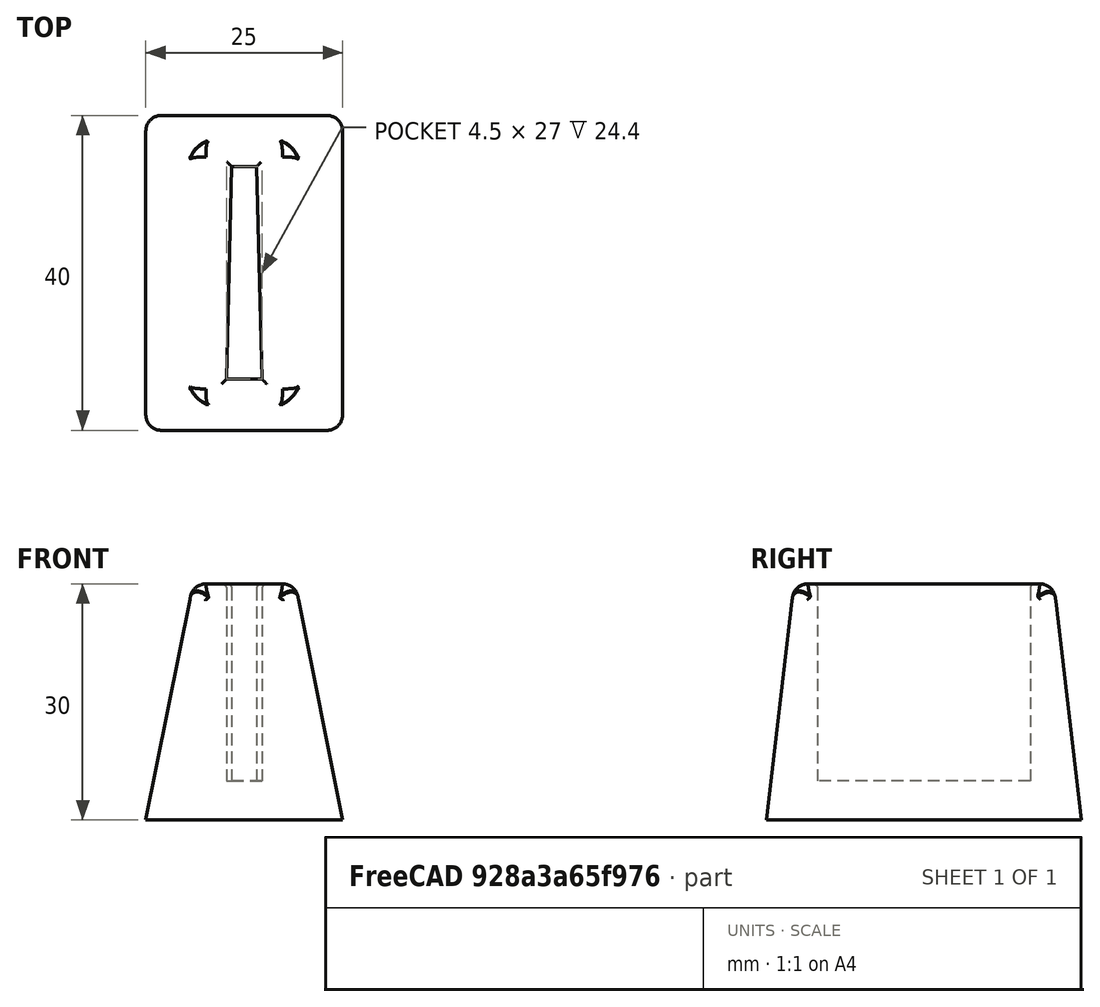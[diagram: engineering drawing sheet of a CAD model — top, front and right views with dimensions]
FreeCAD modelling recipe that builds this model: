
FCSTD DOCUMENT  (FreeCAD 0.18R16117 (Git))
Label: Porte peigne
License: All rights reserved
LicenseURL: http://en.wikipedia.org/wiki/All_rights_reserved
objects: Sketcher::SketchObject×3, PartDesign::Fillet×3, PartDesign::Pocket×2, PartDesign::Pad×1, PartDesign::Body×1
note: 13 computed .brp shape members not serialized (recipe doc carries the construction recipe); baked Part::Feature solids carry a one-line shape summary decoded from their .brp

FEATURE [Sketcher::SketchObject] Sketch
  MapMode = 5
  Placement = pos=(0,0,0) rot=(1,0,0;1.5708rad)
  Support = -> [XZ_Plane]
  sketch-geometry (6):
    g0: LineSegment StartX=-12.5 StartY=0 StartZ=0 EndX=12.5 EndY=0 EndZ=0
    g1: LineSegment StartX=12.5 StartY=0 StartZ=0 EndX=6.5 EndY=30 EndZ=0
    g2: LineSegment StartX=6.5 StartY=30 StartZ=0 EndX=-6.5 EndY=30 EndZ=0
    g3: LineSegment StartX=-6.5 StartY=30 StartZ=0 EndX=-12.5 EndY=0 EndZ=0
    g4: LineSegment [constr] StartX=-6.5 StartY=30 StartZ=0 EndX=0 EndY=30 EndZ=0
    g5: LineSegment [constr] StartX=-12.5 StartY=0 StartZ=0 EndX=0 EndY=0 EndZ=0
  constraints (17):
    c: Coincident(g0,g1)
    c: Coincident(g1,g2)
    c: Coincident(g2,g3)
    c: Coincident(g3,g0)
    c: Parallel(g2,g0)
    c: Horizontal(g0)
    c: DistanceX(g0,g0) = 25
    c: DistanceX(g2,g2) = 13
    c: DistanceY(g0,g1) = 30
    c: Coincident(g5,g0)
    c: Coincident(g4,g2)
    c: Distance(g4) = 6.5
    c: Horizontal(g4)
    c: Distance(g5) = 12.5
    c: Horizontal(g5)
    c: Vertical(g5,g4)
    c: Coincident(g5,g-1)
FEATURE [PartDesign::Pad] Pad
  Length = 40
  Length2 = 100
  Placement = pos=(0,0,0) rot=(1,0,0;1.5708rad)
  Profile = -> Sketch
  Type = 0
FEATURE [Sketcher::SketchObject] Sketch001
  ExternalGeometry = -> [Pad]
  MapMode = 5
  Placement = pos=(0,2e-14,30) rot=(0,0,1;3.14159rad)
  Support = -> [Pad]
  sketch-geometry (6):
    g0: LineSegment StartX=-2.25 StartY=33.5 StartZ=0 EndX=2.25 EndY=33.5 EndZ=0
    g1: LineSegment StartX=2.25 StartY=33.5 StartZ=0 EndX=1.575 EndY=6.5 EndZ=0
    g2: LineSegment StartX=1.575 StartY=6.5 StartZ=0 EndX=-1.575 EndY=6.5 EndZ=0
    g3: LineSegment StartX=-1.575 StartY=6.5 StartZ=0 EndX=-2.25 EndY=33.5 EndZ=0
    g4: LineSegment [constr] StartX=-2.25 StartY=33.5 StartZ=0 EndX=9e-16 EndY=33.5 EndZ=0
    g5: LineSegment [constr] StartX=-1.575 StartY=6.5 StartZ=0 EndX=9e-16 EndY=6.5 EndZ=0
  constraints (18):
    c: Coincident(g0,g1)
    c: Coincident(g1,g2)
    c: Coincident(g2,g3)
    c: Coincident(g3,g0)
    c: DistanceX(g2,g2) = 3.15
    c: Horizontal(g0)
    c: Horizontal(g2)
    c: DistanceX(g0,g0) = 4.5
    c: Coincident(g5,g2)
    c: Distance(g5) = 1.575
    c: Horizontal(g5)
    c: Coincident(g4,g0)
    c: Distance(g4) = 2.25
    c: Horizontal(g4)
    c: Vertical(g4,g5)
    c: DistanceX(g-3,g5) = 6.5
    c: DistanceY(g5,g4) = 27
    c: DistanceY(g4,g-4) = 6.5
FEATURE [PartDesign::Pocket] Pocket
  BaseFeature = -> Pad
  Length = 25
  Length2 = 100
  Placement = pos=(0,0,0) rot=(1,0,0;1.5708rad)
  Profile = -> Sketch001
  Type = 0
FEATURE [Sketcher::SketchObject] Sketch002
  ExternalGeometry = -> [Pocket]
  MapMode = 5
  Placement = pos=(0,0,0) rot=(0.57735,0.57735,0.57735;2.0944rad)
  Support = -> [YZ_Plane]
  sketch-geometry (8):
    g0: LineSegment StartX=-40 StartY=2.84e-14 StartZ=0 EndX=-36.5 EndY=30 EndZ=0
    g1: LineSegment StartX=-36.5 StartY=30 StartZ=0 EndX=-3.5 EndY=30 EndZ=0
    g2: LineSegment StartX=-3.5 StartY=30 StartZ=0 EndX=-4e-16 EndY=0 EndZ=0
    g3: LineSegment StartX=-4e-16 StartY=0 StartZ=0 EndX=-40 EndY=2.84e-14 EndZ=0
    g4: LineSegment StartX=-50 StartY=40 StartZ=0 EndX=10 EndY=40 EndZ=0
    g5: LineSegment StartX=10 StartY=40 StartZ=0 EndX=10 EndY=-10 EndZ=0
    g6: LineSegment StartX=10 StartY=-10 StartZ=0 EndX=-50 EndY=-10 EndZ=0
    g7: LineSegment StartX=-50 StartY=-10 StartZ=0 EndX=-50 EndY=40 EndZ=0
  constraints (22):
    c: Coincident(g0,g1)
    c: Coincident(g1,g2)
    c: Coincident(g2,g3)
    c: Coincident(g3,g0)
    c: Horizontal(g1)
    c: Coincident(g0,g-4)
    c: Coincident(g2,g-1)
    c: DistanceX(g-5,g0) = 3.5
    c: DistanceX(g1,g-5) = 3.5
    c: PointOnObject(g0,g-5)
    c: Coincident(g4,g5)
    c: Coincident(g5,g6)
    c: Coincident(g6,g7)
    c: Coincident(g7,g4)
    c: Horizontal(g4)
    c: Horizontal(g6)
    c: Vertical(g5)
    c: Vertical(g7)
    c: DistanceX(g2,g5) = 10
    c: DistanceY(g5,g2) = 10
    c: DistanceX(g6,g0) = 10
    c: DistanceY(g1,g4) = 10
FEATURE [PartDesign::Pocket] Pocket001
  BaseFeature = -> Pocket
  Length = 5
  Length2 = 100
  Midplane = true
  Placement = pos=(0,0,0) rot=(1,0,0;1.5708rad)
  Profile = -> Sketch002
  Type = 1
FEATURE [PartDesign::Fillet] Fillet
  Base = -> Pocket001 [Edge11,Edge9,Edge7,Edge12]
  BaseFeature = -> Pocket001
  Placement = pos=(0,0,0) rot=(1,0,0;1.5708rad)
  Radius = 2
FEATURE [PartDesign::Fillet] Fillet001
  Base = -> Fillet [Edge7,Edge18,Edge5,Edge1]
  BaseFeature = -> Fillet
  Placement = pos=(0,0,0) rot=(1,0,0;1.5708rad)
  Radius = 2
FEATURE [PartDesign::Fillet] Fillet002
  Base = -> Fillet001 [Edge57,Edge58,Edge59,Edge60]
  BaseFeature = -> Fillet001
  Placement = pos=(0,0,0) rot=(1,0,0;1.5708rad)
  Radius = 0.6
FEATURE [PartDesign::Body] Body
  Group = -> [Sketch,Pad,Sketch001,Pocket,Sketch002,Pocket001,Fillet,Fillet001,Fillet002]
  Origin = -> Origin
  Tip = -> Fillet002
